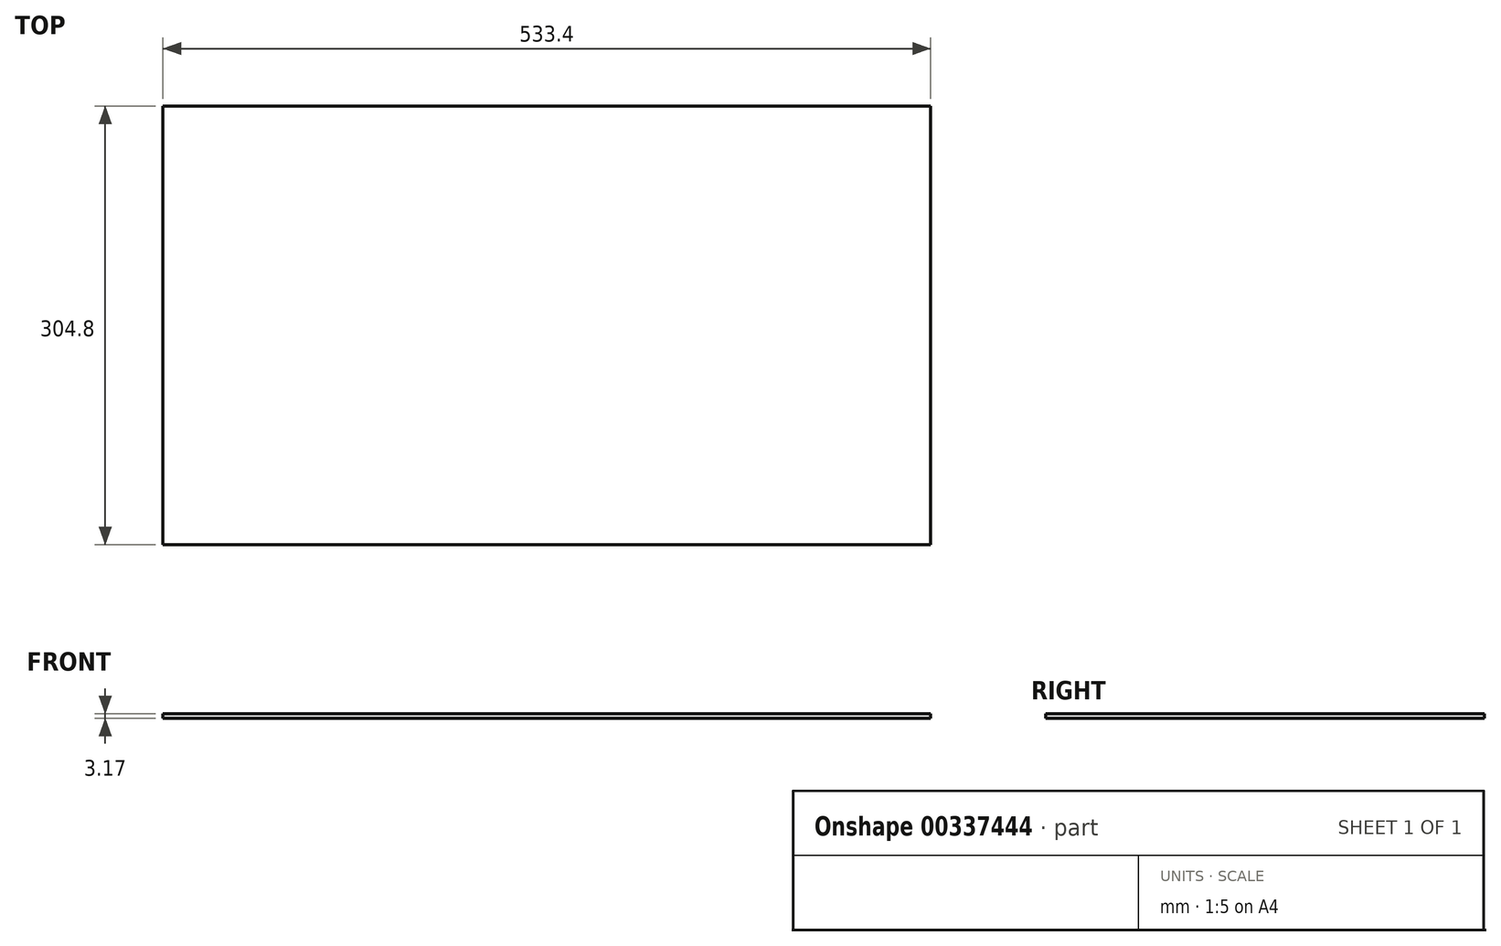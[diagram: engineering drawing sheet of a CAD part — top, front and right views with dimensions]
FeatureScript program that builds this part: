
annotation { "Feature Type Name" : "Feature", "Feature Type Description" : "" }
export const myFeature = defineFeature(function(context is Context, id is Id, definition is map)
    precondition{}
    {
        {
            var Q0;
            Q0=qCreatedBy(makeId("Top.planeOp"),FACE);
            var sketch = newSketch(context, id + "F0", { "sketchPlane" : qUnion([Q0])});
            skLineSegment(sketch, "E0.bottom", {"start": v(-266.7, 152.4) * mm, "end": v(266.7, 152.4) * mm});
            skLineSegment(sketch, "E0.top", {"start": v(-266.7, -152.4) * mm, "end": v(266.7, -152.4) * mm});
            skLineSegment(sketch, "E0.left", {"start": v(-266.7, 152.4) * mm, "end": v(-266.7, -152.4) * mm});
            skLineSegment(sketch, "E0.right", {"start": v(266.7, 152.4) * mm, "end": v(266.7, -152.4) * mm});
            skPoint(sketch, "E0.middle", {"position": v(0, 0) * mm});
            skSolve(sketch);
        }
        {
            var Q0;
            Q0=makeQuery(id+"F0.imprint","IMPRINT",FACE,{"disambiguationData":[TD([[makeQuery(id+"F0.imprint","IMPRINT",EDGE,{"derivedFrom":sQuery(id+"F0.wireOp",EDGE,"E0.bottom")}),-1.0]])]});
            extrude(context, id + "F1", {"entities" : qUnion([Q0]), "depth" : 3.17 * mm});
        }
    });
